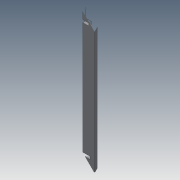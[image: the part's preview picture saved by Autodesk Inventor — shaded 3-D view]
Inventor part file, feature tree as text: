
AUTODESK INVENTOR PART (.ipt)
format: ipt  version: 2015 (Build 190159000, 159)  size: 85,504 bytes
history: native  units: mm
features: extrude x1, sketch x1
ambient origin geometry x8: Origin, YZ Plane, XZ Plane, XY Plane, X Axis, Y Axis, Z Axis, Center Point
bodies: Body1 (feature_tree)
feature tree (2):
  extrude  "Extrusion5"  Depth=9.0mm
  sketch  "Sketch2"  dims[d25=40.0mm d31=9.0mm d32=20.0mm d33=30.0mm d38=30.0mm d39=9.0mm d40=25.0mm d41=9.0mm d42=0.0mm d43=400.0mm]
